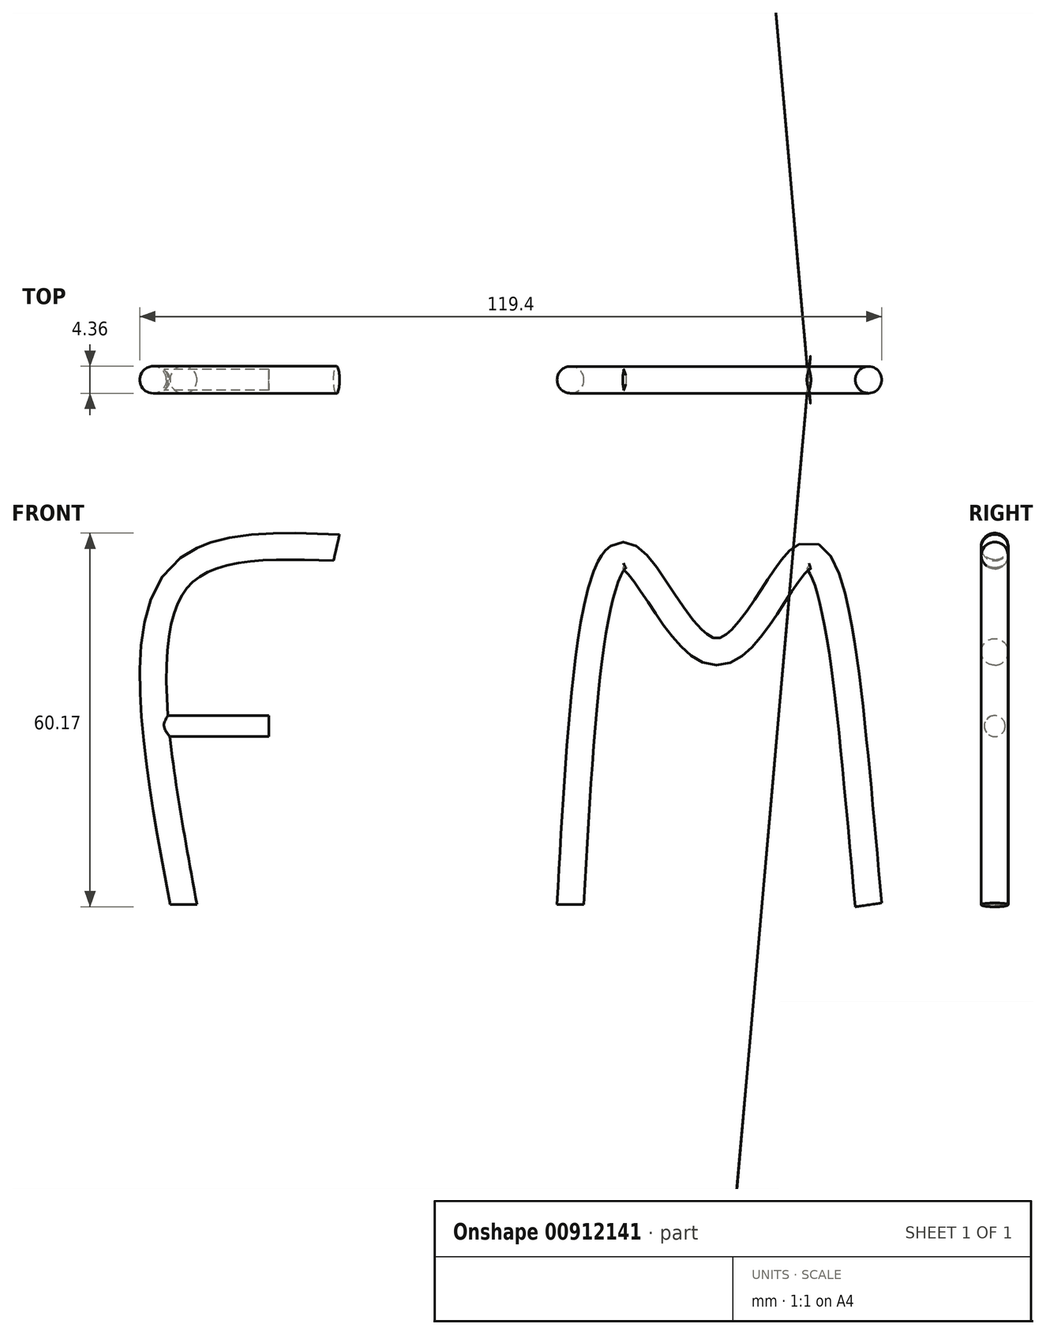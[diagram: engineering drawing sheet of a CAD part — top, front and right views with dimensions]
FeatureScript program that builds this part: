
annotation { "Feature Type Name" : "Feature", "Feature Type Description" : "" }
export const myFeature = defineFeature(function(context is Context, id is Id, definition is map)
    precondition{}
    {
        {
            var Q0;
            Q0=qCreatedBy(makeId("Front.planeOp"),FACE);
            var sketch = newSketch(context, id + "F0", { "sketchPlane" : qUnion([Q0])});
            skFitSpline(sketch, "E0", {"points": [v(-48.91, 0) * mm, v(-50, 52.47) * mm, v(-23.7, 57.95) * mm], "startDerivative": vector(-20.8, 112.42) * mm, "endDerivative": vector(76.61, -2.9) * mm});
            skLineSegment(sketch, "E1", {"start": v(-53.4, 28.8) * mm, "end": v(-34.71, 28.8) * mm});
            skFitSpline(sketch, "E2", {"points": [v(13.56, 0) * mm, v(23.15, 56.3) * mm, v(37.4, 40.96) * mm, v(51.38, 56.3) * mm, v(62.06, 0) * mm], "startDerivative": vector(14.96, 287.3) * mm, "endDerivative": vector(26.51, -281.95) * mm});
            skSolve(sketch);
        }
        {
            var Q0;
            Q0=qCreatedBy(makeId("Top.planeOp"),FACE);
            var sketch = newSketch(context, id + "F1", { "sketchPlane" : qUnion([Q0])});
            skCircle(sketch, "E3", {"center": v(-48.43, 0) * mm, "radius": 2.18 * mm});
            skCircle(sketch, "E4", {"center": v(13.84, 0) * mm, "radius": 2.15 * mm});
            skSolve(sketch);
        }
        {
            var Q0;
            Q0=makeQuery(id+"F1.imprint","IMPRINT",FACE,{"disambiguationData":[TD([[makeQuery(id+"F1.imprint","IMPRINT",EDGE,{"derivedFrom":sQuery(id+"F1.wireOp",EDGE,"E3")}),1.0]])]});
            var Q1;
            Q1=sQuery(id+"F0.wireOp",EDGE,"E0");
            sweep(context, id + "F2", {"profiles" : qUnion([Q0]), "path" : qUnion([Q1])});
        }
        {
            var Q0;
            Q0=makeQuery(id+"F1.imprint","IMPRINT",FACE,{"disambiguationData":[TD([[makeQuery(id+"F1.imprint","IMPRINT",EDGE,{"derivedFrom":sQuery(id+"F1.wireOp",EDGE,"E4")}),1.0]])]});
            var Q1;
            Q1=sQuery(id+"F0.wireOp",EDGE,"E2");
            sweep(context, id + "F3", {"profiles" : qUnion([Q0]), "path" : qUnion([Q1])});
        }
        {
            var Q0;
            Q0=sQuery(id+"F0.wireOp",VERTEX,"E1.end");
            var Q1;
            Q1=sQuery(id+"F0.wireOp",EDGE,"E1");
            cPlane(context, id + "F4", {"entities" : qUnion([Q0, Q1]), "cplaneType" : CPlaneType.CURVE_POINT, "offset" : 25.4 * mm, "width" : 152.4 * mm, "height" : 152.4 * mm});
        }
        {
            var Q0;
            Q0=qCreatedBy(id+"F4.planeOp",FACE);
            var sketch = newSketch(context, id + "F5", { "sketchPlane" : qUnion([Q0])});
            skCircle(sketch, "E5", {"center": v(0, 28.75) * mm, "radius": 1.68 * mm});
            skSolve(sketch);
        }
        {
            var Q0;
            Q0=makeQuery(id+"F5.imprint","IMPRINT",FACE,{"disambiguationData":[TD([[makeQuery(id+"F5.imprint","IMPRINT",EDGE,{"derivedFrom":sQuery(id+"F5.wireOp",EDGE,"E5")}),1.0]])]});
            var Q1;
            Q1=sQuery(id+"F0.wireOp",EDGE,"E1");
            sweep(context, id + "F6", {"operationType" : NewBodyOperationType.ADD, "profiles" : qUnion([Q0]), "path" : qUnion([Q1])});
        }
    });
